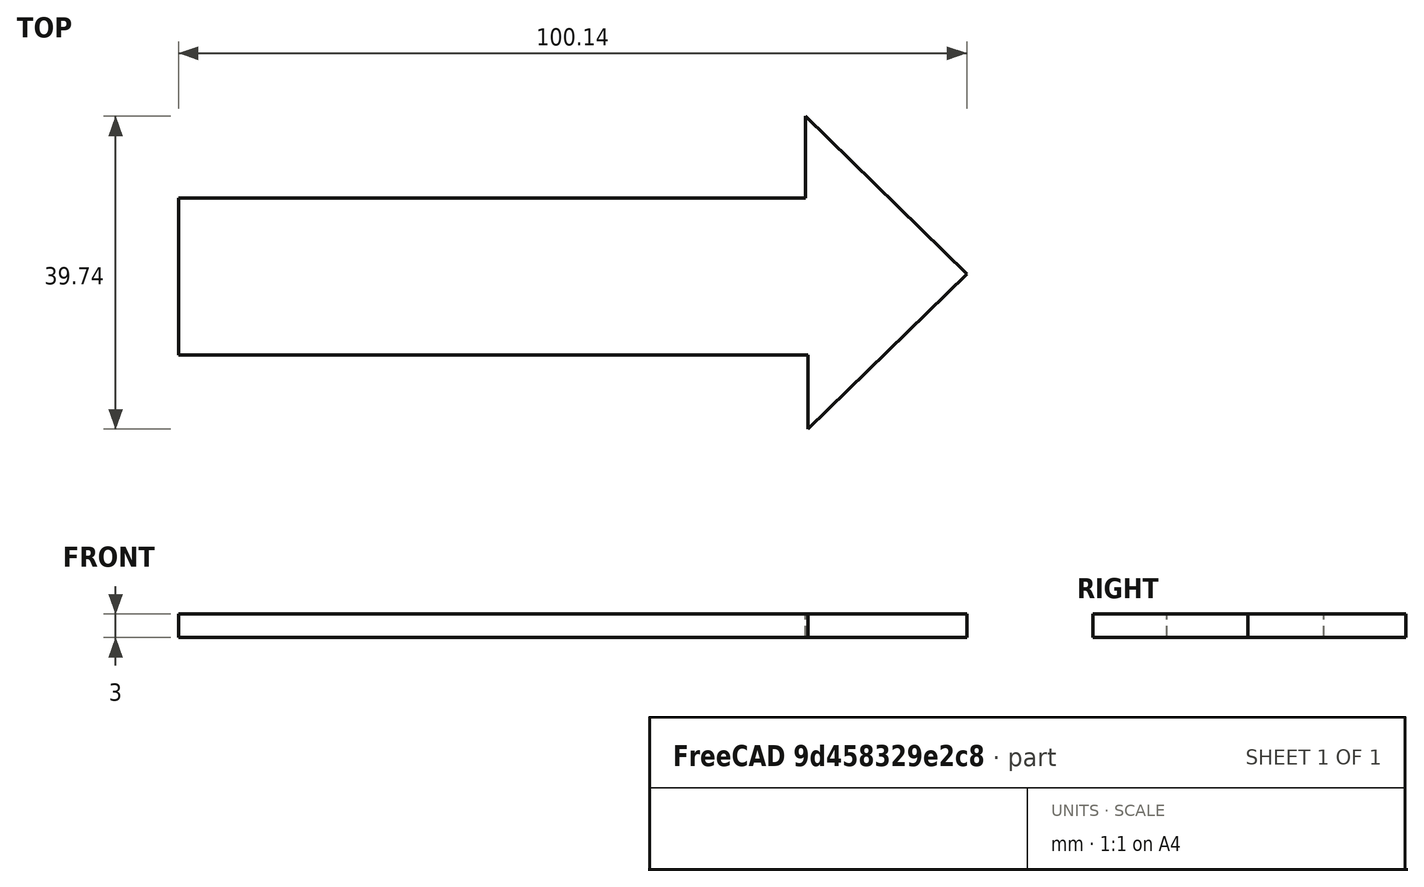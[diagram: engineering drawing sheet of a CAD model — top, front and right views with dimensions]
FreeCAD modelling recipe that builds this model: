
FCSTD DOCUMENT  (FreeCAD 1.0R39319 (Git))
Label: ojt16r02_arrow
License: All rights reserved
LicenseURL: https://en.wikipedia.org/wiki/All_rights_reserved
objects: Sketcher::SketchObject×1, PartDesign::Pad×1, PartDesign::Body×1
note: 6 computed .brp shape members not serialized (recipe doc carries the construction recipe); baked Part::Feature solids carry a one-line shape summary decoded from their .brp

FEATURE [Sketcher::SketchObject] Sketch
  ArcFitTolerance = 1e-06
  AttachmentSupport = -> [XY_Plane]
  FullyConstrained = false
  MakeInternals = false
  MapMode = 5
  sketch-geometry (7):
    g0: LineSegment StartX=-39.9059 StartY=-10.2635 StartZ=0 EndX=40.0188 EndY=-10.2635 EndZ=0
    g1: LineSegment StartX=40.0188 StartY=-10.2635 StartZ=0 EndX=40.0188 EndY=-19.6797 EndZ=0
    g2: LineSegment StartX=40.0188 StartY=-19.6797 StartZ=0 EndX=60.2259 EndY=0 EndZ=0
    g3: LineSegment StartX=60.2259 StartY=0 StartZ=0 EndX=39.6986 EndY=20.0567 EndZ=0
    g4: LineSegment StartX=39.6986 StartY=20.0567 StartZ=0 EndX=39.6986 EndY=9.69885 EndZ=0
    g5: LineSegment StartX=39.6986 StartY=9.69885 StartZ=0 EndX=-39.9059 EndY=9.69885 EndZ=0
    g6: LineSegment StartX=-39.9059 StartY=9.69885 StartZ=0 EndX=-39.9059 EndY=-10.2635 EndZ=0
  constraints (13):
    c: Horizontal(g0)
    c: Coincident(g0,g1)
    c: Vertical(g1)
    c: Coincident(g1,g2)
    c: PointOnObject(g2,g-1)
    c: Coincident(g2,g3)
    c: Coincident(g3,g4)
    c: Vertical(g4)
    c: Coincident(g4,g5)
    c: Horizontal(g5)
    c: Coincident(g5,g6)
    c: Coincident(g6,g0)
    c: Vertical(g6)
FEATURE [PartDesign::Pad] Pad
  Direction = (0,0,1)
  Length = 3
  Length2 = 10
  Profile = -> Sketch
  ReferenceAxis = -> Sketch [N_Axis]
  Refine = true
  Suppressed = false
  Type = 0
FEATURE [PartDesign::Body] Body  label="Cos"
  AllowCompound = false
  Group = -> [Sketch,Pad]
  Origin = -> Origin
  Tip = -> Pad
